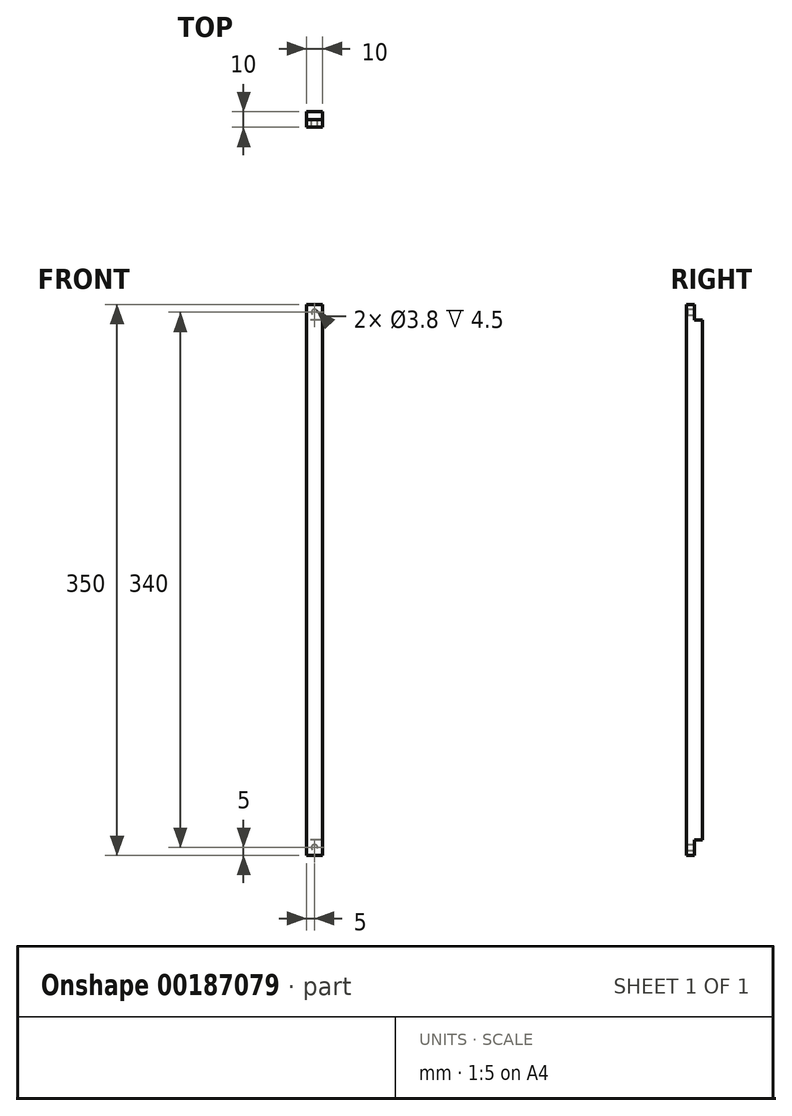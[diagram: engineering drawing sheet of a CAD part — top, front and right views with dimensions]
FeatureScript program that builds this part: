
annotation { "Feature Type Name" : "Feature", "Feature Type Description" : "" }
export const myFeature = defineFeature(function(context is Context, id is Id, definition is map)
    precondition{}
    {
        {
            var Q0;
            Q0=qCreatedBy(makeId("Right.planeOp"),FACE);
            var sketch = newSketch(context, id + "F0", { "sketchPlane" : qUnion([Q0])});
            skLineSegment(sketch, "E0", {"start": v(0, 0) * mm, "end": v(0, 165) * mm});
            skLineSegment(sketch, "E1", {"start": v(0, 165) * mm, "end": v(-5, 165) * mm});
            skLineSegment(sketch, "E2", {"start": v(-5, 165) * mm, "end": v(-5, 175) * mm});
            skLineSegment(sketch, "E3", {"start": v(-5, 175) * mm, "end": v(-10, 175) * mm});
            skLineSegment(sketch, "E4", {"start": v(-10, 175) * mm, "end": v(-10, 0) * mm});
            skLineSegment(sketch, "E5", {"start": v(-10, 0) * mm, "end": v(0, 0) * mm});
            skSolve(sketch);
        }
        {
            var Q0;
            Q0 = qSketchRegion(id + "F0", true);
            extrude(context, id + "F1", {"entities" : qUnion([Q0]), "depth" : 10 * mm});
        }
        {
            var Q0;
            Q0=makeQuery(id+"F1.opExtrude","SWEPT_FACE",FACE,{"disambiguationData":[OSD([sQuery(id+"F0.wireOp",EDGE,"E2")])]});
            var sketch = newSketch(context, id + "F2", { "sketchPlane" : qUnion([Q0])});
            skCircle(sketch, "E6", {"center": v(-5, 170) * mm, "radius": 1.9 * mm});
            skPoint(sketch, "E6.centerSnap0", {"position": v(-5, 175) * mm});
            skPoint(sketch, "E6.centerSnap1", {"position": v(0, 170) * mm});
            skSolve(sketch);
        }
        {
            var Q0;
            Q0 = qSketchRegion(id + "F2", true);
            extrude(context, id + "F3", {"entities" : qUnion([Q0]), "operationType" : NewBodyOperationType.REMOVE, "oppositeDirection" : true, "depth" : 4.5 * mm});
        }
        {
            var Q0;
            Q0=makeQuery(id+"F1.opExtrude","SWEPT_BODY",BODY,{"disambiguationData":[OSD([sQuery(id+"F0.wireOp",EDGE,"E0"),sQuery(id+"F0.wireOp",EDGE,"E1"),sQuery(id+"F0.wireOp",EDGE,"E2"),sQuery(id+"F0.wireOp",EDGE,"E3"),sQuery(id+"F0.wireOp",EDGE,"E4"),sQuery(id+"F0.wireOp",EDGE,"E5")])]});
            var Q1;
            Q1=qCreatedBy(makeId("Top.planeOp"),FACE);
            mirror(context, id + "F4", {"operationType" : NewBodyOperationType.ADD, "entities" : qUnion([Q0]), "mirrorPlane" : qUnion([Q1])});
        }
    });
